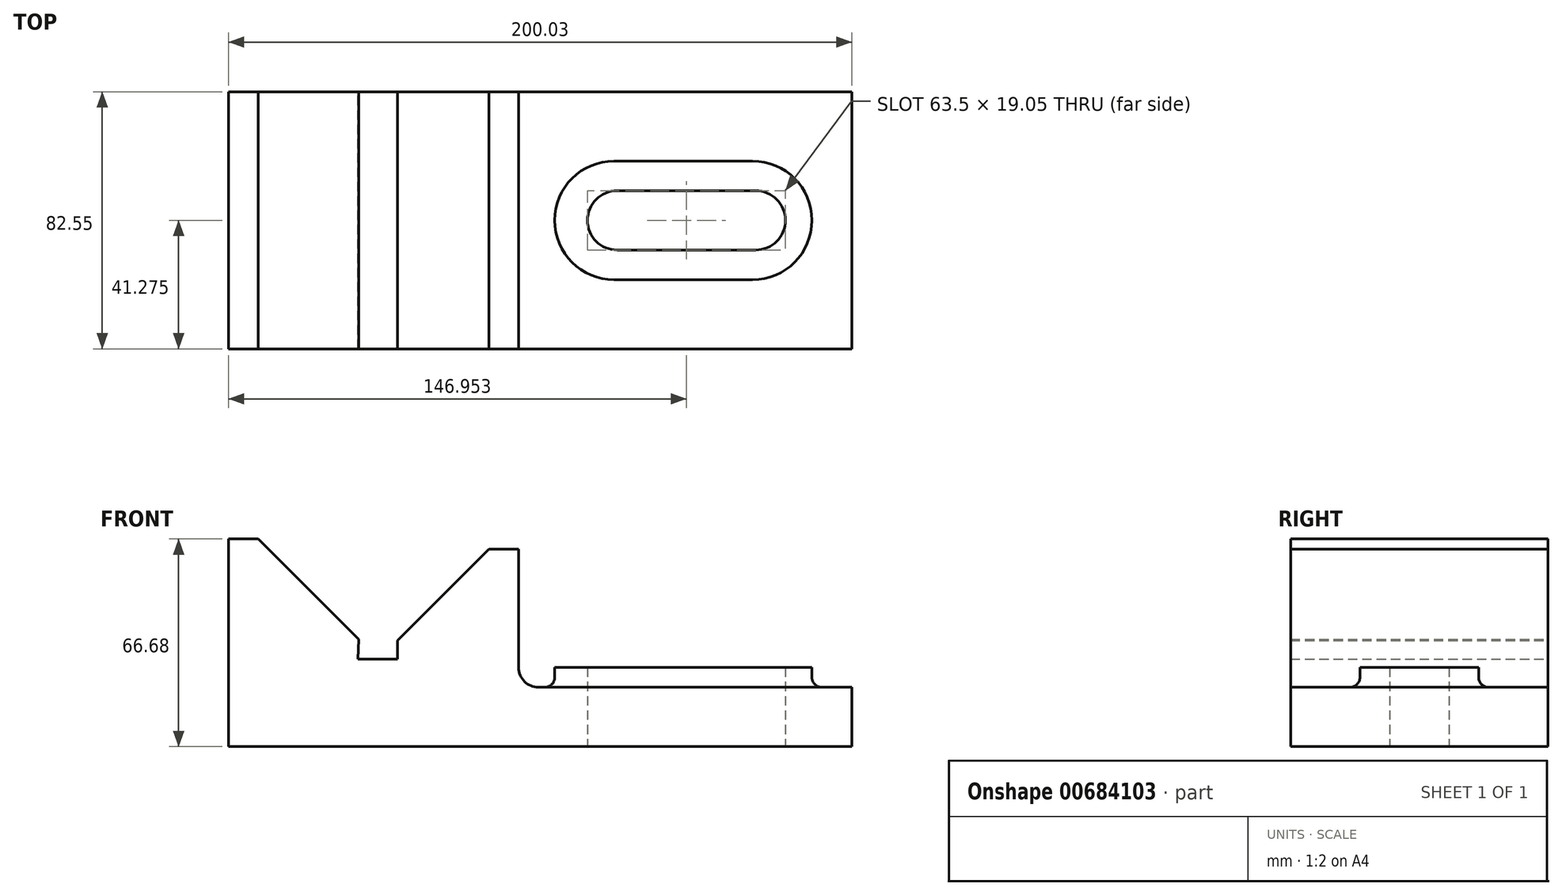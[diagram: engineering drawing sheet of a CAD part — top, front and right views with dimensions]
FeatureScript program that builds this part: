
annotation { "Feature Type Name" : "Feature", "Feature Type Description" : "" }
export const myFeature = defineFeature(function(context is Context, id is Id, definition is map)
    precondition{}
    {
        {
            var Q0;
            Q0=qCreatedBy(makeId("Front.planeOp"),FACE);
            var sketch = newSketch(context, id + "F0", { "sketchPlane" : qUnion([Q0])});
            skLineSegment(sketch, "E0.bottom", {"start": v(0, 0) * mm, "end": v(200.03, 0) * mm});
            skLineSegment(sketch, "E0.left", {"start": v(0, 0) * mm, "end": v(0, 66.68) * mm});
            skLineSegment(sketch, "E0.right", {"start": v(200.03, 0) * mm, "end": v(200.03, 19.05) * mm});
            skLineSegment(sketch, "E1.top", {"start": v(200.03, 19.05) * mm, "end": v(93.12, 19.05) * mm});
            skLineSegment(sketch, "E1.right", {"start": v(93.12, 63.41) * mm, "end": v(93.12, 19.05) * mm});
            skLineSegment(sketch, "E2", {"start": v(9.53, 66.68) * mm, "end": v(41.8, 34.4) * mm});
            skLineSegment(sketch, "E3.trimOffspring", {"start": v(83.6, 63.41) * mm, "end": v(93.12, 63.41) * mm});
            skLineSegment(sketch, "E4", {"start": v(0, 66.68) * mm, "end": v(9.53, 66.68) * mm});
            skLineSegment(sketch, "E5", {"start": v(83.6, 63.41) * mm, "end": v(54.24, 34.06) * mm});
            skLineSegment(sketch, "E6", {"start": v(54.24, 34.06) * mm, "end": v(54.24, 28.05) * mm});
            skLineSegment(sketch, "E7", {"start": v(54.24, 28.05) * mm, "end": v(41.54, 28.05) * mm});
            skLineSegment(sketch, "E8", {"start": v(41.54, 28.05) * mm, "end": v(41.8, 34.4) * mm});
            skSolve(sketch);
        }
        {
            var Q0;
            Q0 = qSketchRegion(id + "F0", true);
            extrude(context, id + "F1", {"entities" : qUnion([Q0]), "depth" : 82.55 * mm, "offsetDistance" : 25 * mm});
        }
        {
            var Q0;
            Q0=qCreatedBy(makeId("Top.planeOp"),FACE);
            var sketch = newSketch(context, id + "F2", { "sketchPlane" : qUnion([Q0])});
            skLineSegment(sketch, "E9.bottom", {"start": v(123.73, -22.23) * mm, "end": v(168.18, -22.23) * mm});
            skLineSegment(sketch, "E9.top", {"start": v(123.73, -60.33) * mm, "end": v(168.18, -60.33) * mm});
            skArc(sketch, "E10", {"start": v(123.73, -22.23) * mm, "mid": v(104.68, -41.28) * mm, "end": v(123.73, -60.33) * mm});
            skArc(sketch, "E11", {"start": v(168.18, -60.33) * mm, "mid": v(187.23, -41.28) * mm, "end": v(168.18, -22.23) * mm});
            skSolve(sketch);
        }
        {
            var Q0;
            Q0 = qSketchRegion(id + "F2", true);
            extrude(context, id + "F3", {"entities" : qUnion([Q0]), "operationType" : NewBodyOperationType.ADD, "depth" : 25.4 * mm, "offsetDistance" : 25.4 * mm});
        }
        {
            var Q0;
            Q0=qCreatedBy(makeId("Top.planeOp"),FACE);
            var sketch = newSketch(context, id + "F4", { "sketchPlane" : qUnion([Q0])});
            skLineSegment(sketch, "E12.bottom", {"start": v(124.73, -50.8) * mm, "end": v(169.18, -50.8) * mm});
            skLineSegment(sketch, "E12.top", {"start": v(124.73, -31.75) * mm, "end": v(169.18, -31.75) * mm});
            skArc(sketch, "E13", {"start": v(169.18, -50.8) * mm, "mid": v(178.7, -41.28) * mm, "end": v(169.18, -31.75) * mm});
            skArc(sketch, "E14", {"start": v(124.73, -31.75) * mm, "mid": v(115.2, -41.28) * mm, "end": v(124.73, -50.8) * mm});
            skSolve(sketch);
        }
        {
            var Q0;
            Q0 = qSketchRegion(id + "F4", true);
            extrude(context, id + "F5", {"entities" : qUnion([Q0]), "operationType" : NewBodyOperationType.REMOVE, "endBound" : BoundingType.THROUGH_ALL, "depth" : 25.4 * mm, "offsetDistance" : 25.4 * mm});
        }
        {
            var Q0;
            Q0=makeQuery(id+"F3.boolean.opBoolean","INTERSECT",EDGE,{"derivedFrom":[makeQuery(id+"F1.opExtrude","SWEPT_FACE",FACE,{"disambiguationData":[OSD([sQuery(id+"F0.wireOp",EDGE,"E1.top")])]}),makeQuery(id+"F3.opExtrude","SWEPT_FACE",FACE,{"disambiguationData":[OSD([sQuery(id+"F2.wireOp",EDGE,"E9.top")])]})]});
            fillet(context, id + "F6", {"entities" : qUnion([Q0]), "radius" : 3.17 * mm, "tangentPropagation" : true, "allowEdgeOverflow" : false});
        }
        {
            var Q0;
            Q0=makeQuery(id+"F1.opExtrude","SWEPT_EDGE",EDGE,{"disambiguationData":[OSD([sQuery(id+"F0.wireOp",EDGE,"E1.top"),sQuery(id+"F0.wireOp",EDGE,"E1.right")])]});
            fillet(context, id + "F7", {"entities" : qUnion([Q0]), "radius" : 6.35 * mm, "tangentPropagation" : true, "allowEdgeOverflow" : false});
        }
    });
